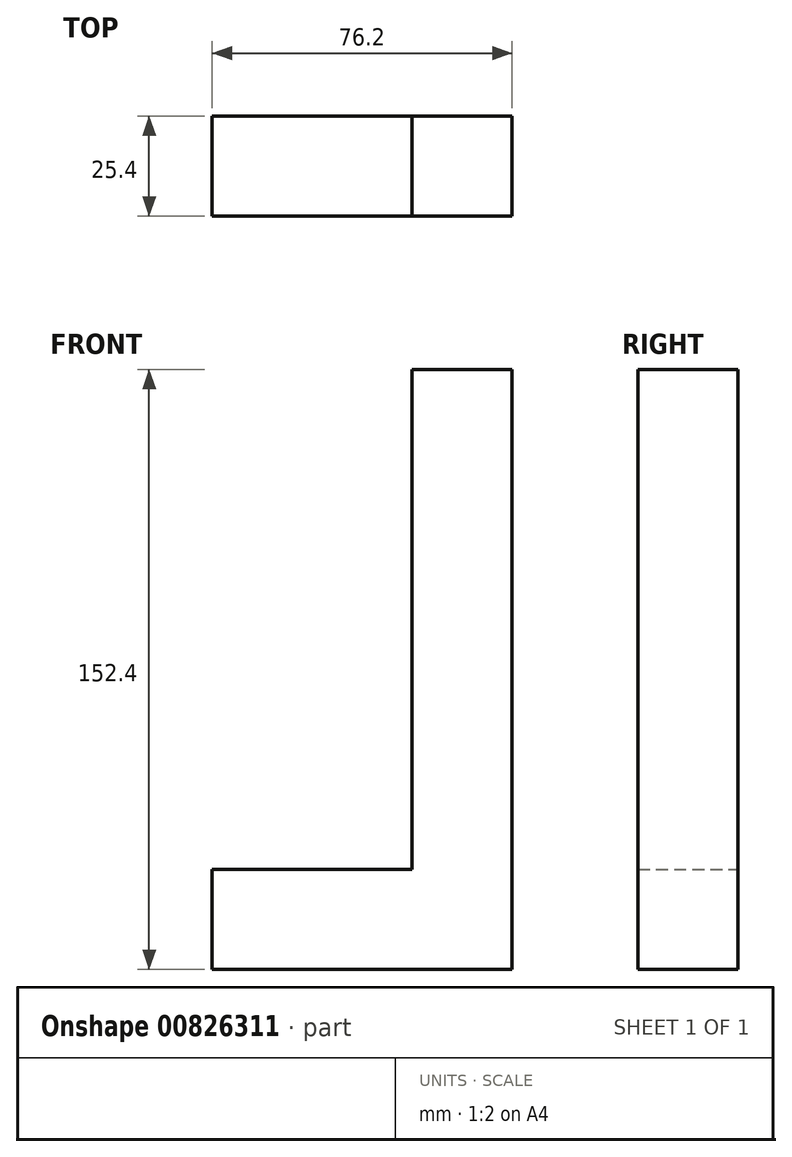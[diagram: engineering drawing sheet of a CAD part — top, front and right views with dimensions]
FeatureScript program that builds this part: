
annotation { "Feature Type Name" : "Feature", "Feature Type Description" : "" }
export const myFeature = defineFeature(function(context is Context, id is Id, definition is map)
    precondition{}
    {
        {
            var Q0;
            Q0=qCreatedBy(makeId("Front.planeOp"),FACE);
            var sketch = newSketch(context, id + "F0", { "sketchPlane" : qUnion([Q0])});
            skLineSegment(sketch, "E0", {"start": v(0, 0) * mm, "end": v(0, 152.4) * mm});
            skLineSegment(sketch, "E1", {"start": v(0, 152.4) * mm, "end": v(-25.4, 152.4) * mm});
            skLineSegment(sketch, "E2", {"start": v(-25.4, 152.4) * mm, "end": v(-25.4, 25.4) * mm});
            skLineSegment(sketch, "E3", {"start": v(-25.4, 25.4) * mm, "end": v(-76.2, 25.4) * mm});
            skLineSegment(sketch, "E4", {"start": v(-76.2, 25.4) * mm, "end": v(-76.2, 0) * mm});
            skLineSegment(sketch, "E5", {"start": v(-76.2, 0) * mm, "end": v(0, 0) * mm});
            skSolve(sketch);
        }
        {
            var Q0;
            Q0=makeQuery(id+"F0.imprint","IMPRINT",FACE,{"disambiguationData":[TD([[makeQuery(id+"F0.imprint","IMPRINT",EDGE,{"derivedFrom":sQuery(id+"F0.wireOp",EDGE,"E0")}),1.0]])]});
            extrude(context, id + "F1", {"entities" : qUnion([Q0]), "depth" : 25.4 * mm, "offsetDistance" : 25.4 * mm});
        }
    });
